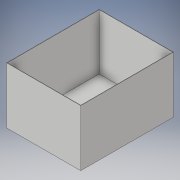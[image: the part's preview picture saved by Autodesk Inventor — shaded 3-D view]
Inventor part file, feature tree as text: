
AUTODESK INVENTOR PART (.ipt)
format: ipt  version: 2018 (Build 220112000, 112)  size: 113,152 bytes
history: native  units: in
note: dims shown in document units (in); Inventor stores cm internally (conversion verified against a paired STEP export)
features: extrude x3, sketch x3
ambient origin geometry x8: Origin, YZ Plane, XZ Plane, XY Plane, X Axis, Y Axis, Z Axis, Center Point
bodies: Solid1 (feature_tree)
feature tree (6):
  extrude  "Extrusion1"  Depth=5.0in
  extrude  "Extrusion2"  Depth=3.96in
  extrude  "Extrusion3"  Depth=3.0in TaperAngle=0.0deg
  sketch  "Sketch1"  dims[d0=4.0in d1=5.0in]
  sketch  "Sketch2"  dims[d2=0.04in d3=0.0in d4=3.96in]
  sketch  "Sketch3"  dims[d5=4.96in d6=3.0in d7=0.0in d8=1.0in d9=2.0in d10=0.164in d11=0.164in d12=0.0in d13=0.0in]
